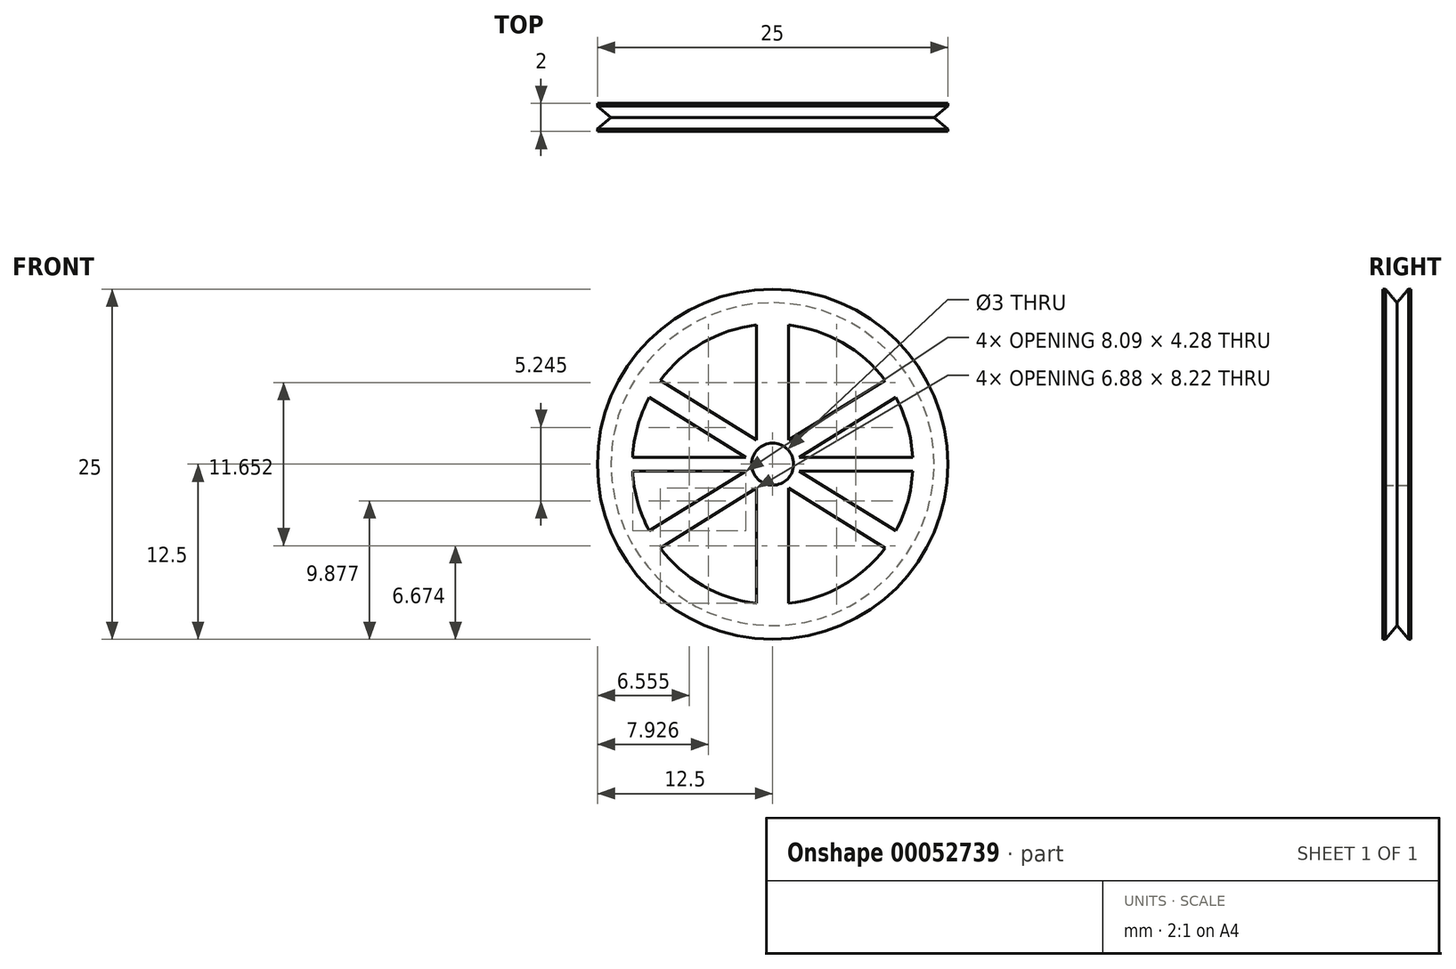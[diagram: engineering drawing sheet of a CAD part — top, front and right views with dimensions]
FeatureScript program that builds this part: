
annotation { "Feature Type Name" : "Feature", "Feature Type Description" : "" }
export const myFeature = defineFeature(function(context is Context, id is Id, definition is map)
    precondition{}
    {
        {
            var Q0;
            Q0=qCreatedBy(makeId("Front.planeOp"),FACE);
            var sketch = newSketch(context, id + "F0", { "sketchPlane" : qUnion([Q0])});
            skCircle(sketch, "E0", {"center": v(0, 0) * mm, "radius": 12.5 * mm});
            skCircle(sketch, "E1", {"center": v(0, 0) * mm, "radius": 10 * mm});
            skCircle(sketch, "E2", {"center": v(0, 0) * mm, "radius": 1.5 * mm});
            skLineSegment(sketch, "E3", {"start": v(0, 1.72) * mm, "end": v(-1.14, 1.72) * mm});
            skLineSegment(sketch, "E4.MirrorCS", {"start": v(0, 1.72) * mm, "end": v(1.14, 1.72) * mm});
            skLineSegment(sketch, "E5.MirrorCS", {"start": v(0, -1.72) * mm, "end": v(1.14, -1.72) * mm});
            skLineSegment(sketch, "E6.MirrorCS", {"start": v(0, -1.72) * mm, "end": v(-1.14, -1.72) * mm});
            skLineSegment(sketch, "E7", {"start": v(-1.14, 1.72) * mm, "end": v(-1.9, 0.48) * mm});
            skLineSegment(sketch, "E8.MirrorCS", {"start": v(1.14, 1.72) * mm, "end": v(1.9, 0.48) * mm});
            skLineSegment(sketch, "E9.MirrorCS", {"start": v(-1.14, -1.72) * mm, "end": v(-1.9, -0.48) * mm});
            skLineSegment(sketch, "E10.MirrorCS", {"start": v(1.14, -1.72) * mm, "end": v(1.9, -0.48) * mm});
            skLineSegment(sketch, "E11", {"start": v(-1.9, 0.48) * mm, "end": v(-1.9, -0.48) * mm});
            skLineSegment(sketch, "E12", {"start": v(1.9, 0.48) * mm, "end": v(1.9, -0.48) * mm});
            skLineSegment(sketch, "E13", {"start": v(-1.14, 1.72) * mm, "end": v(-1.14, 9.94) * mm});
            skLineSegment(sketch, "E14", {"start": v(-1.14, 9.94) * mm, "end": v(-1.14, 1.72) * mm});
            skLineSegment(sketch, "E15", {"start": v(1.14, 1.72) * mm, "end": v(1.14, 9.94) * mm});
            skLineSegment(sketch, "E16", {"start": v(1.14, 9.94) * mm, "end": v(1.14, 1.72) * mm});
            skLineSegment(sketch, "E17", {"start": v(1.14, 1.72) * mm, "end": v(8.01, 5.98) * mm});
            skLineSegment(sketch, "E18", {"start": v(1.9, 0.48) * mm, "end": v(8.8, 4.76) * mm});
            skLineSegment(sketch, "E19", {"start": v(1.9, 0.48) * mm, "end": v(9.99, 0.48) * mm});
            skLineSegment(sketch, "E20", {"start": v(1.9, -0.48) * mm, "end": v(9.99, -0.48) * mm});
            skLineSegment(sketch, "E21", {"start": v(1.14, -1.72) * mm, "end": v(8.01, -5.98) * mm});
            skLineSegment(sketch, "E22", {"start": v(1.9, -0.48) * mm, "end": v(8.8, -4.76) * mm});
            skLineSegment(sketch, "E23", {"start": v(-1.14, -1.72) * mm, "end": v(-1.14, -9.94) * mm});
            skLineSegment(sketch, "E24", {"start": v(1.14, -1.72) * mm, "end": v(1.14, -9.94) * mm});
            skLineSegment(sketch, "E25", {"start": v(-1.14, 1.72) * mm, "end": v(-8.01, 5.98) * mm});
            skLineSegment(sketch, "E26", {"start": v(-1.9, 0.48) * mm, "end": v(-8.8, 4.76) * mm});
            skLineSegment(sketch, "E27.MirrorCS", {"start": v(-1.9, 0.48) * mm, "end": v(-9.99, 0.48) * mm});
            skLineSegment(sketch, "E28.MirrorCS", {"start": v(-1.9, -0.48) * mm, "end": v(-9.99, -0.48) * mm});
            skLineSegment(sketch, "E29", {"start": v(-1.9, -0.48) * mm, "end": v(-8.8, -4.76) * mm});
            skLineSegment(sketch, "E30", {"start": v(-1.14, -1.72) * mm, "end": v(-8.01, -5.98) * mm});
            skSolve(sketch);
        }
        {
            var Q0;
            Q0=makeQuery(id+"F0.imprint","IMPRINT",FACE,{"disambiguationData":[TD([[makeQuery(id+"F0.imprint","IMPRINT",EDGE,{"derivedFrom":sQuery(id+"F0.wireOp",EDGE,"E7")}),-1.0]])]});
            var Q1;
            Q1=makeQuery(id+"F0.imprint","IMPRINT",FACE,{"disambiguationData":[TD([[makeQuery(id+"F0.imprint","IMPRINT",EDGE,{"derivedFrom":sQuery(id+"F0.wireOp",EDGE,"E2")}),-1.0]])]});
            var Q2;
            Q2=makeQuery(id+"F0.imprint","IMPRINT",FACE,{"disambiguationData":[TD([[makeQuery(id+"F0.imprint","IMPRINT",EDGE,{"derivedFrom":sQuery(id+"F0.wireOp",EDGE,"E3")}),-1.0]])]});
            var Q3;
            Q3=makeQuery(id+"F0.imprint","IMPRINT",FACE,{"disambiguationData":[TD([[makeQuery(id+"F0.imprint","IMPRINT",EDGE,{"derivedFrom":sQuery(id+"F0.wireOp",EDGE,"E8.MirrorCS")}),1.0]])]});
            var Q4;
            Q4=makeQuery(id+"F0.imprint","IMPRINT",FACE,{"disambiguationData":[TD([[makeQuery(id+"F0.imprint","IMPRINT",EDGE,{"derivedFrom":sQuery(id+"F0.wireOp",EDGE,"E12")}),1.0]])]});
            var Q5;
            Q5=makeQuery(id+"F0.imprint","IMPRINT",FACE,{"disambiguationData":[TD([[makeQuery(id+"F0.imprint","IMPRINT",EDGE,{"derivedFrom":sQuery(id+"F0.wireOp",EDGE,"E10.MirrorCS")}),-1.0]])]});
            var Q6;
            Q6=makeQuery(id+"F0.imprint","IMPRINT",FACE,{"disambiguationData":[TD([[makeQuery(id+"F0.imprint","IMPRINT",EDGE,{"derivedFrom":sQuery(id+"F0.wireOp",EDGE,"E5.MirrorCS")}),-1.0]])]});
            var Q7;
            Q7=makeQuery(id+"F0.imprint","IMPRINT",FACE,{"disambiguationData":[TD([[makeQuery(id+"F0.imprint","IMPRINT",EDGE,{"derivedFrom":sQuery(id+"F0.wireOp",EDGE,"E9.MirrorCS")}),1.0]])]});
            var Q8;
            Q8=makeQuery(id+"F0.imprint","IMPRINT",FACE,{"disambiguationData":[TD([[makeQuery(id+"F0.imprint","IMPRINT",EDGE,{"derivedFrom":sQuery(id+"F0.wireOp",EDGE,"E11")}),-1.0]])]});
            var Q9;
            Q9=makeQuery(id+"F0.imprint","IMPRINT",FACE,{"disambiguationData":[TD([[makeQuery(id+"F0.imprint","IMPRINT",EDGE,{"derivedFrom":sQuery(id+"F0.wireOp",EDGE,"E0")}),1.0]])]});
            extrude(context, id + "F1", {"entities" : qUnion([Q0, Q1, Q2, Q3, Q4, Q5, Q6, Q7, Q8, Q9]), "endBound" : BoundingType.SYMMETRIC, "depth" : 2 * mm});
        }
        {
            var Q0;
            Q0=qCreatedBy(makeId("Right.planeOp"),FACE);
            var sketch = newSketch(context, id + "F2", { "sketchPlane" : qUnion([Q0])});
            skLineSegment(sketch, "E31", {"start": v(0, 12.5) * mm, "end": v(-0.82, 12.5) * mm});
            skLineSegment(sketch, "E32", {"start": v(-0.82, 12.5) * mm, "end": v(0, 11.53) * mm});
            skLineSegment(sketch, "E33", {"start": v(0, 11.53) * mm, "end": v(0, 12.5) * mm});
            skLineSegment(sketch, "E34.MirrorCS", {"start": v(0, 12.5) * mm, "end": v(0.82, 12.5) * mm});
            skLineSegment(sketch, "E35.MirrorCS", {"start": v(0.82, 12.5) * mm, "end": v(0, 11.53) * mm});
            skLineSegment(sketch, "E36", {"start": v(-9.95, 0) * mm, "end": v(10.68, 0) * mm, "construction": true});
            skSolve(sketch);
        }
        {
            var Q0;
            Q0 = qSketchRegion(id + "F2", true);
            var Q1;
            Q1=sQuery(id+"F2.wireOp",EDGE,"E36");
            revolve(context, id + "F3", {"operationType" : NewBodyOperationType.REMOVE, "entities" : qUnion([Q0]), "axis" : qUnion([Q1]), "revolveType" : RevolveType.FULL, "oppositeDirection" : true});
        }
    });
